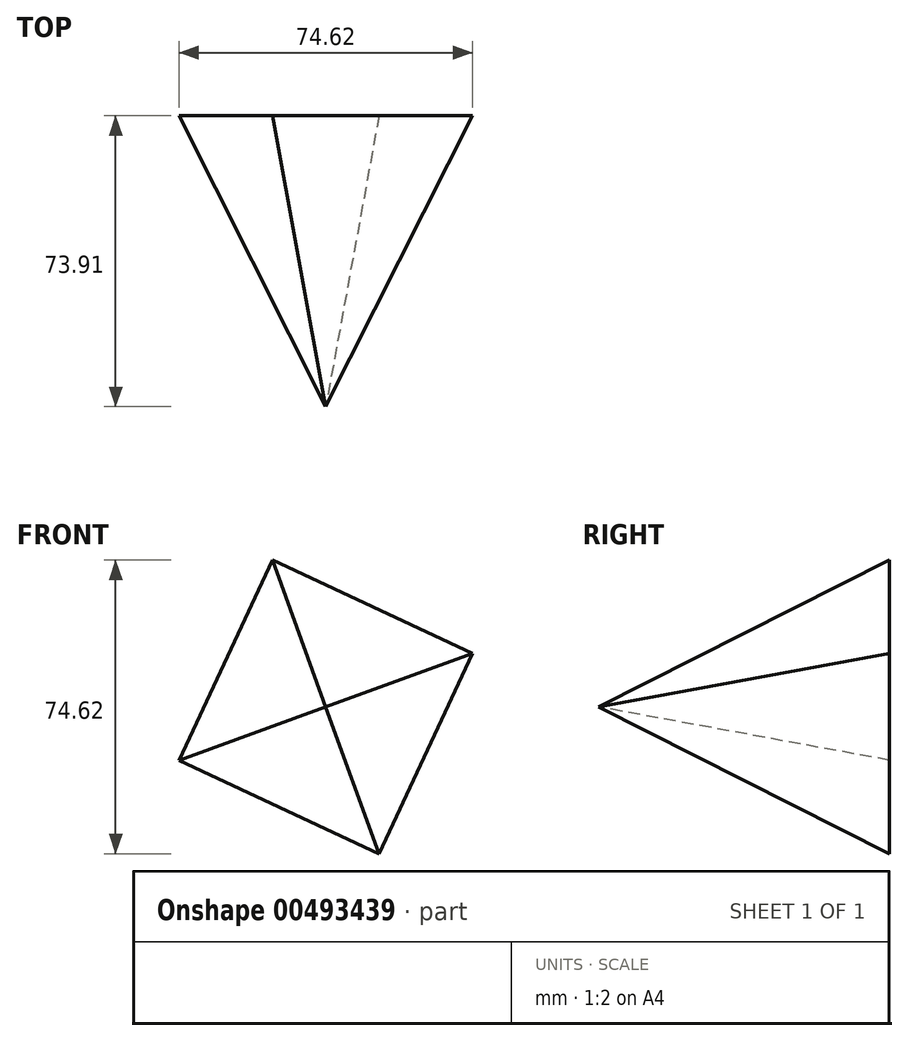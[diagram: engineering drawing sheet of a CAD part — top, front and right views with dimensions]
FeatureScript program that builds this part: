
annotation { "Feature Type Name" : "Feature", "Feature Type Description" : "" }
export const myFeature = defineFeature(function(context is Context, id is Id, definition is map)
    precondition{}
    {
        {
            var Q0;
            Q0=qCreatedBy(makeId("Front.planeOp"),FACE);
            var sketch = newSketch(context, id + "F0", { "sketchPlane" : qUnion([Q0])});
            skCircle(sketch, "E0.cCircle", {"center": v(0, 0) * mm, "radius": 39.7 * mm, "construction": true});
            skLineSegment(sketch, "E0.0", {"start": v(37.3, 13.55) * mm, "end": v(13.55, -37.3) * mm});
            skLineSegment(sketch, "E0.1", {"start": v(13.55, -37.3) * mm, "end": v(-37.3, -13.55) * mm});
            skLineSegment(sketch, "E0.2", {"start": v(-37.3, -13.55) * mm, "end": v(-13.55, 37.3) * mm});
            skLineSegment(sketch, "E0.3", {"start": v(-13.55, 37.3) * mm, "end": v(37.3, 13.55) * mm});
            skSolve(sketch);
        }
        {
            var Q0;
            Q0=qCreatedBy(makeId("Front.planeOp"),FACE);
            cPlane(context, id + "F1", {"entities" : qUnion([Q0]), "cplaneType" : CPlaneType.OFFSET, "offset" : 73.9 * mm, "width" : 152.4 * mm, "height" : 152.4 * mm});
        }
        {
            var Q0;
            Q0=qCreatedBy(id+"F1.planeOp",FACE);
            var sketch = newSketch(context, id + "F2", { "sketchPlane" : qUnion([Q0])});
            skCircle(sketch, "E1", {"center": v(0, 0) * mm, "radius": 3.76 * mm});
            skSolve(sketch);
        }
        {
            var Q0;
            Q0=makeQuery(id+"F0.imprint","IMPRINT",FACE,{"disambiguationData":[TD([[makeQuery(id+"F0.imprint","IMPRINT",EDGE,{"derivedFrom":sQuery(id+"F0.wireOp",EDGE,"E0.0")}),-1.0]])]});
            var Q1;
            Q1=sQuery(id+"F2.wireOp",VERTEX,"E1.center");
            loft(context, id + "F3", {"sheetProfilesArray" : [{ "sheetProfileEntities" : qUnion([Q0]) }, { "sheetProfileEntities" : qUnion([Q1]) }]});
        }
    });
